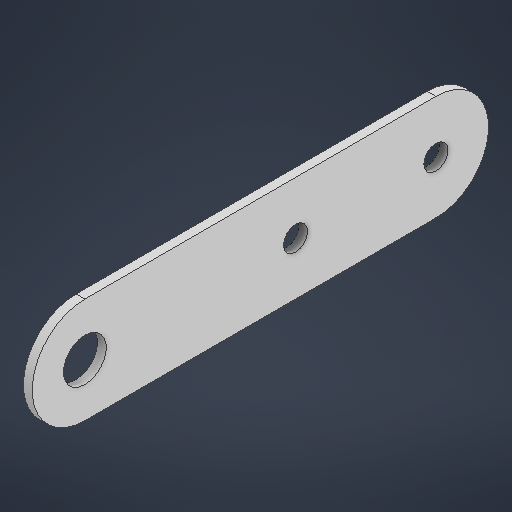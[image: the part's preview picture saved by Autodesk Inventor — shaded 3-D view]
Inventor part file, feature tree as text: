
AUTODESK INVENTOR PART (.ipt)
format: ipt  version: 2025.2 (Build 292293000, 293)  size: 186,880 bytes
history: native  units: in
note: dims shown in document units (in); Inventor stores cm internally (conversion verified against a paired STEP export)
features: extrude x1, sketch x1
ambient origin geometry x8: Origin, YZ Plane, XZ Plane, XY Plane, X Axis, Y Axis, Z Axis, Center Point
bodies: Solid1 (feature_tree)
feature tree (2):
  extrude  "Extrusion1"  Depth=0.75in
  sketch  "Sketch1"  dims[d0=0.305in d1=0.75in d2=0.172in d3=2.5in d4=0.75in d6=0.0625in d7=0.0in d9=0.172in]
